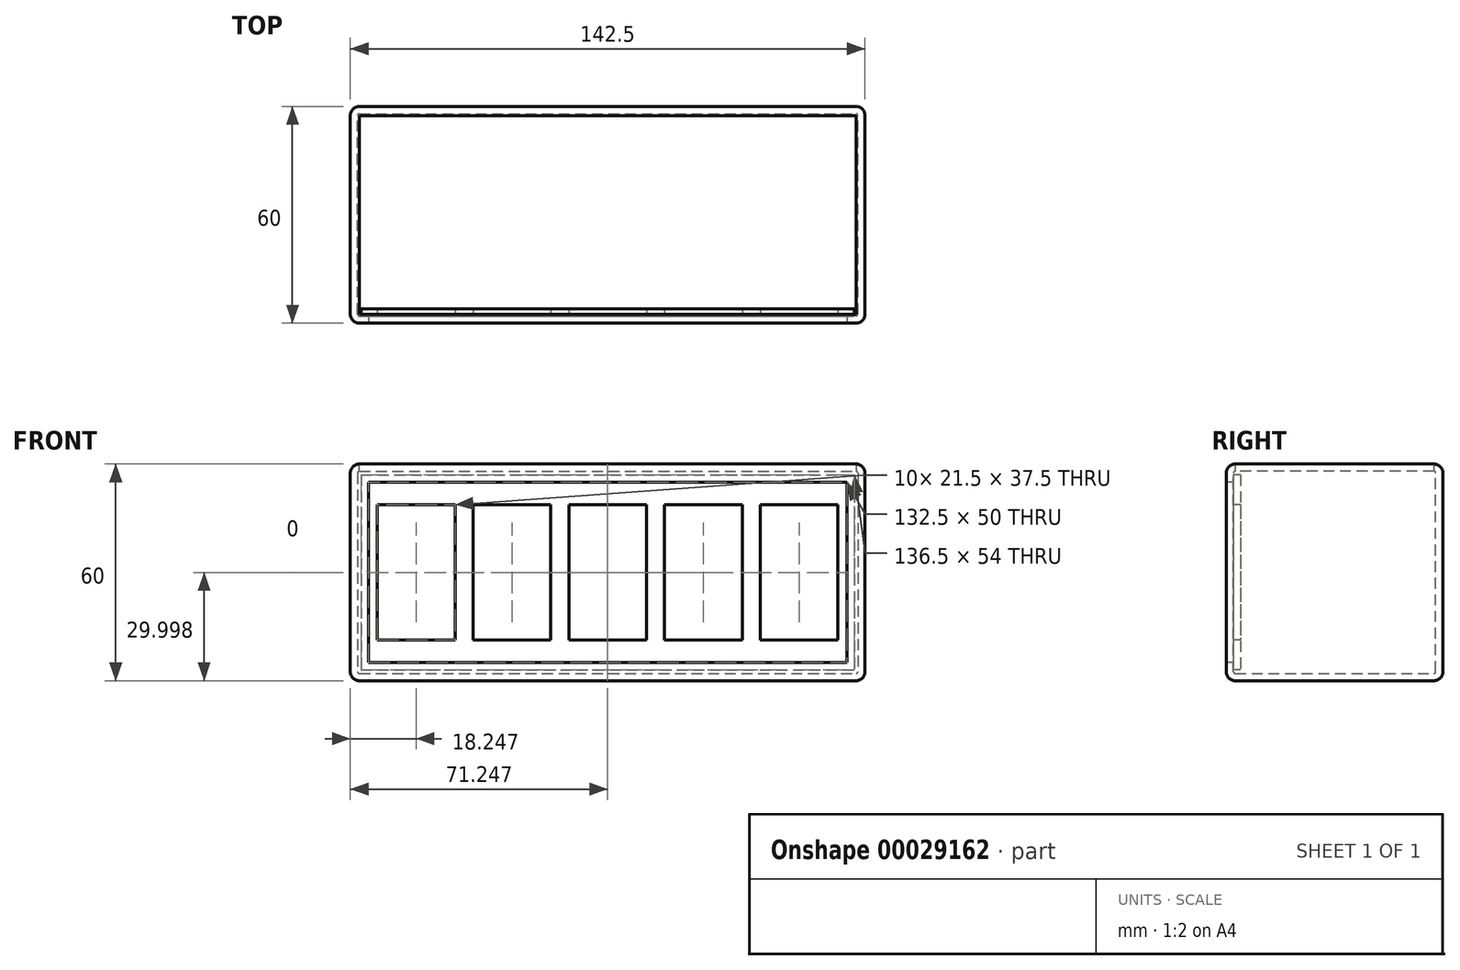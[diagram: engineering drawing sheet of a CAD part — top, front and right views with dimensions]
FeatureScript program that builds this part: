
annotation { "Feature Type Name" : "Feature", "Feature Type Description" : "" }
export const myFeature = defineFeature(function(context is Context, id is Id, definition is map)
    precondition{}
    {
        {
            var Q0;
            Q0=qCreatedBy(makeId("Front.planeOp"),FACE);
            var sketch = newSketch(context, id + "F0", { "sketchPlane" : qUnion([Q0])});
            skLineSegment(sketch, "E0.bottom", {"start": v(-76.53, 18.7) * mm, "end": v(65.97, 18.7) * mm});
            skLineSegment(sketch, "E0.top", {"start": v(-76.53, -41.3) * mm, "end": v(65.97, -41.3) * mm});
            skLineSegment(sketch, "E0.left", {"start": v(-76.53, 18.7) * mm, "end": v(-76.53, -41.3) * mm});
            skLineSegment(sketch, "E0.right", {"start": v(65.97, 18.7) * mm, "end": v(65.97, -41.3) * mm});
            skSolve(sketch);
        }
        {
            var Q0;
            Q0 = qSketchRegion(id + "F0", true);
            extrude(context, id + "F5", {"entities" : qUnion([Q0]), "depth" : 60 * mm});
        }
        {
            var Q0;
            Q0=makeQuery(id+"F5.opExtrude","CAP_EDGE",EDGE,{"disambiguationData":[OSD([sQuery(id+"F0.wireOp",EDGE,"E0.left")])],"isStart":false});
            var Q1;
            Q1=makeQuery(id+"F5.opExtrude","CAP_EDGE",EDGE,{"disambiguationData":[OSD([sQuery(id+"F0.wireOp",EDGE,"E0.top")])],"isStart":false});
            var Q2;
            Q2=makeQuery(id+"F5.opExtrude","CAP_EDGE",EDGE,{"disambiguationData":[OSD([sQuery(id+"F0.wireOp",EDGE,"E0.right")])],"isStart":false});
            var Q3;
            Q3=makeQuery(id+"F5.opExtrude","CAP_EDGE",EDGE,{"disambiguationData":[OSD([sQuery(id+"F0.wireOp",EDGE,"E0.bottom")])],"isStart":false});
            var Q4;
            Q4=makeQuery(id+"F5.opExtrude","SWEPT_FACE",FACE,{"disambiguationData":[OSD([sQuery(id+"F0.wireOp",EDGE,"E0.top")])]});
            var Q5;
            Q5=makeQuery(id+"F5.opExtrude","CAP_FACE",FACE,{"disambiguationData":[OSD([sQuery(id+"F0.wireOp",EDGE,"E0.bottom"),sQuery(id+"F0.wireOp",EDGE,"E0.top"),sQuery(id+"F0.wireOp",EDGE,"E0.left"),sQuery(id+"F0.wireOp",EDGE,"E0.right")])],"isStart":true});
            var Q6;
            Q6=makeQuery(id+"F5.opExtrude","SWEPT_FACE",FACE,{"disambiguationData":[OSD([sQuery(id+"F0.wireOp",EDGE,"E0.right")])]});
            var Q7;
            Q7=makeQuery(id+"F5.opExtrude","SWEPT_FACE",FACE,{"disambiguationData":[OSD([sQuery(id+"F0.wireOp",EDGE,"E0.left")])]});
            fillet(context, id + "F6", {"entities" : qUnion([Q0, Q1, Q2, Q3, Q4, Q5, Q6, Q7]), "radius" : 2.5 * mm, "tangentPropagation" : true, "allowEdgeOverflow" : false});
        }
        {
            var Q0;
            Q0=makeQuery(id+"F5.opExtrude","CAP_FACE",FACE,{"disambiguationData":[OSD([sQuery(id+"F0.wireOp",EDGE,"E0.bottom"),sQuery(id+"F0.wireOp",EDGE,"E0.top"),sQuery(id+"F0.wireOp",EDGE,"E0.left"),sQuery(id+"F0.wireOp",EDGE,"E0.right")])],"isStart":false});
            var sketch = newSketch(context, id + "F1", { "sketchPlane" : qUnion([Q0])});
            skLineSegment(sketch, "E1.bottom", {"start": v(-71.53, 13.7) * mm, "end": v(60.97, 13.7) * mm});
            skLineSegment(sketch, "E1.top", {"start": v(-71.53, -36.3) * mm, "end": v(60.97, -36.3) * mm});
            skLineSegment(sketch, "E1.left", {"start": v(-71.53, 13.7) * mm, "end": v(-71.53, -36.3) * mm});
            skLineSegment(sketch, "E1.right", {"start": v(60.97, 13.7) * mm, "end": v(60.97, -36.3) * mm});
            skSolve(sketch);
        }
        {
            var Q0;
            Q0=makeQuery(id+"F1.imprint","IMPRINT",FACE,{"disambiguationData":[TD([[makeQuery(id+"F1.imprint","IMPRINT",EDGE,{"derivedFrom":sQuery(id+"F1.wireOp",EDGE,"E1.bottom")}),-1.0]])]});
            extrude(context, id + "F2", {"entities" : qUnion([Q0]), "operationType" : NewBodyOperationType.REMOVE, "oppositeDirection" : true, "depth" : 2 * mm});
        }
        {
            var Q0;
            Q0=makeQuery(id+"F5.opExtrude","SWEPT_FACE",FACE,{"disambiguationData":[OSD([sQuery(id+"F0.wireOp",EDGE,"E0.bottom")])]});
            shell(context, id + "F3", {"entities" : qUnion([Q0]), "thickness" : 2 * mm});
        }
        {
            var Q0;
            Q0=makeQuery(id+"F2.boolean.opBoolean","COPY",FACE,{"derivedFrom":makeQuery(id+"F2.opExtrude","CAP_FACE",FACE,{"disambiguationData":[OSD([sQuery(id+"F1.wireOp",EDGE,"E1.bottom"),sQuery(id+"F1.wireOp",EDGE,"E1.top"),sQuery(id+"F1.wireOp",EDGE,"E1.left"),sQuery(id+"F1.wireOp",EDGE,"E1.right")])],"isStart":false})});
            var sketch = newSketch(context, id + "F4", { "sketchPlane" : qUnion([Q0])});
            skLineSegment(sketch, "E2", {"start": v(-71.07, 7.45) * mm, "end": v(60.97, 7.45) * mm});
            skLineSegment(sketch, "E3", {"start": v(-71.53, -30.05) * mm, "end": v(60.97, -30.05) * mm});
            skLineSegment(sketch, "E4", {"start": v(-69.03, 7.45) * mm, "end": v(-69.03, -30.05) * mm});
            skLineSegment(sketch, "E5", {"start": v(-47.53, 7.45) * mm, "end": v(-47.53, -30.05) * mm});
            skLineSegment(sketch, "E6", {"start": v(-42.53, 7.45) * mm, "end": v(-42.53, -30.05) * mm});
            skLineSegment(sketch, "E7", {"start": v(-21.03, 7.45) * mm, "end": v(-21.03, -30.05) * mm});
            skLineSegment(sketch, "E8", {"start": v(-16.03, 7.45) * mm, "end": v(-16.03, -30.05) * mm});
            skLineSegment(sketch, "E9", {"start": v(5.47, 7.45) * mm, "end": v(5.47, -30.05) * mm});
            skLineSegment(sketch, "E10", {"start": v(10.47, 7.45) * mm, "end": v(10.47, -30.05) * mm});
            skLineSegment(sketch, "E11", {"start": v(31.97, 7.45) * mm, "end": v(31.97, -30.05) * mm});
            skLineSegment(sketch, "E12", {"start": v(36.97, 7.45) * mm, "end": v(36.97, -30.05) * mm});
            skLineSegment(sketch, "E13", {"start": v(58.47, 7.45) * mm, "end": v(58.47, -30.05) * mm});
            skSolve(sketch);
        }
        {
            var Q0;
            {var subQ1=sQuery(id+"F4.wireOp",EDGE,"E4");Q0=makeQuery(id+"F4.imprint","IMPRINT",FACE,{"disambiguationData":[TD([[makeQuery(id+"F4.imprint","IMPRINT",EDGE,{"derivedFrom":subQ1}),1.0]])]});}
            var Q1;
            {var subQ1=sQuery(id+"F4.wireOp",EDGE,"E6");Q1=makeQuery(id+"F4.imprint","IMPRINT",FACE,{"disambiguationData":[TD([[makeQuery(id+"F4.imprint","IMPRINT",EDGE,{"derivedFrom":subQ1}),1.0]])]});}
            var Q2;
            {var subQ1=sQuery(id+"F4.wireOp",EDGE,"E8");Q2=makeQuery(id+"F4.imprint","IMPRINT",FACE,{"disambiguationData":[TD([[makeQuery(id+"F4.imprint","IMPRINT",EDGE,{"derivedFrom":subQ1}),1.0]])]});}
            var Q3;
            {var subQ1=sQuery(id+"F4.wireOp",EDGE,"E10");Q3=makeQuery(id+"F4.imprint","IMPRINT",FACE,{"disambiguationData":[TD([[makeQuery(id+"F4.imprint","IMPRINT",EDGE,{"derivedFrom":subQ1}),1.0]])]});}
            var Q4;
            {var subQ1=sQuery(id+"F4.wireOp",EDGE,"E12");Q4=makeQuery(id+"F4.imprint","IMPRINT",FACE,{"disambiguationData":[TD([[makeQuery(id+"F4.imprint","IMPRINT",EDGE,{"derivedFrom":subQ1}),1.0]])]});}
            extrude(context, id + "F7", {"entities" : qUnion([Q0, Q1, Q2, Q3, Q4]), "operationType" : NewBodyOperationType.REMOVE, "oppositeDirection" : true, "depth" : 25 * mm});
        }
    });
